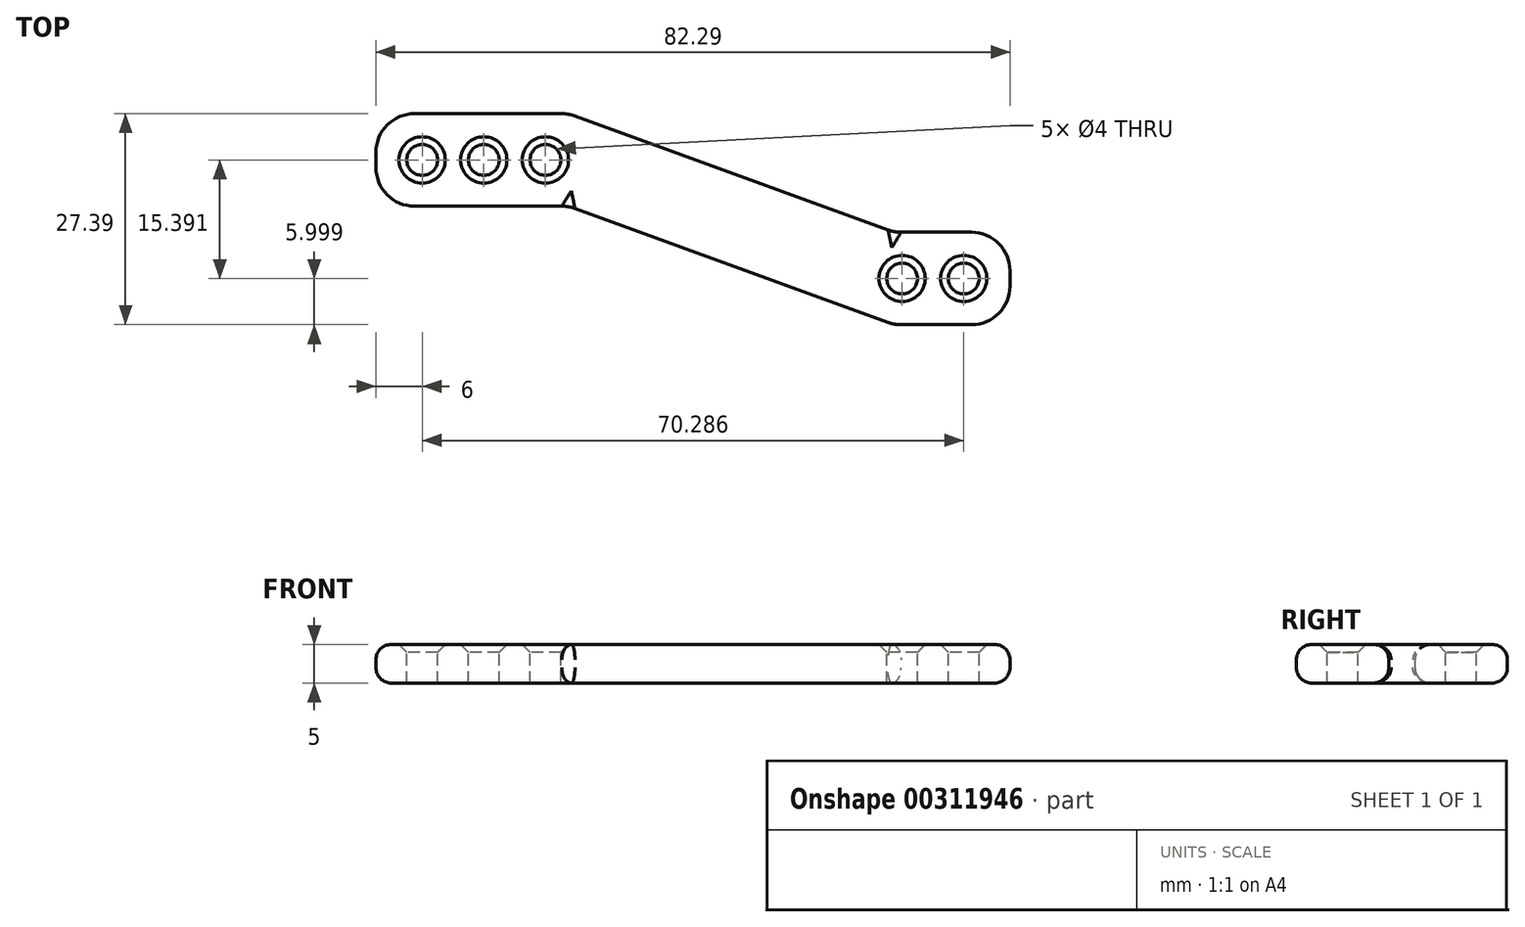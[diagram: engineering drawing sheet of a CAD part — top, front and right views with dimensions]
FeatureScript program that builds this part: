
annotation { "Feature Type Name" : "Feature", "Feature Type Description" : "" }
export const myFeature = defineFeature(function(context is Context, id is Id, definition is map)
    precondition{}
    {
        {
            var Q0;
            Q0=qCreatedBy(makeId("Top.planeOp"),FACE);
            var sketch = newSketch(context, id + "F0", { "sketchPlane" : qUnion([Q0])});
            skLineSegment(sketch, "E0.bottom", {"start": v(0, 0) * mm, "end": v(25, 0) * mm});
            skLineSegment(sketch, "E0.top", {"start": v(0, -12) * mm, "end": v(25, -12) * mm});
            skLineSegment(sketch, "E0.left", {"start": v(0, 0) * mm, "end": v(0, -12) * mm});
            skLineSegment(sketch, "E0.right", {"start": v(25, 0) * mm, "end": v(25, -12) * mm});
            skLineSegment(sketch, "E1.bottom", {"start": v(67.29, -15.4) * mm, "end": v(82.29, -15.4) * mm});
            skLineSegment(sketch, "E1.top", {"start": v(67.29, -27.4) * mm, "end": v(82.29, -27.4) * mm});
            skLineSegment(sketch, "E1.left", {"start": v(67.29, -15.4) * mm, "end": v(67.29, -27.4) * mm});
            skLineSegment(sketch, "E1.right", {"start": v(82.29, -15.4) * mm, "end": v(82.29, -27.4) * mm});
            skLineSegment(sketch, "E2", {"start": v(25, -12) * mm, "end": v(67.29, -27.4) * mm});
            skLineSegment(sketch, "E3", {"start": v(25, 0) * mm, "end": v(67.29, -15.4) * mm});
            skSolve(sketch);
        }
        {
            var Q0;
            Q0=makeQuery(id+"F0.imprint","IMPRINT",FACE,{"disambiguationData":[TD([[makeQuery(id+"F0.imprint","IMPRINT",EDGE,{"derivedFrom":sQuery(id+"F0.wireOp",EDGE,"E0.bottom")}),-1.0]])]});
            var Q1;
            Q1=makeQuery(id+"F0.imprint","IMPRINT",FACE,{"disambiguationData":[TD([[makeQuery(id+"F0.imprint","IMPRINT",EDGE,{"derivedFrom":sQuery(id+"F0.wireOp",EDGE,"E0.right")}),1.0]])]});
            var Q2;
            Q2=makeQuery(id+"F0.imprint","IMPRINT",FACE,{"disambiguationData":[TD([[makeQuery(id+"F0.imprint","IMPRINT",EDGE,{"derivedFrom":sQuery(id+"F0.wireOp",EDGE,"E1.bottom")}),-1.0]])]});
            extrude(context, id + "F1", {"entities" : qUnion([Q0, Q1, Q2]), "depth" : 5 * mm});
        }
        {
            var Q0;
            Q0=makeQuery(id+"F1.opExtrude","CAP_FACE",FACE,{"disambiguationData":[OSD([sQuery(id+"F0.wireOp",EDGE,"E0.bottom"),sQuery(id+"F0.wireOp",EDGE,"E0.top"),sQuery(id+"F0.wireOp",EDGE,"E0.left"),sQuery(id+"F0.wireOp",EDGE,"E1.bottom"),sQuery(id+"F0.wireOp",EDGE,"E1.top"),sQuery(id+"F0.wireOp",EDGE,"E1.right"),sQuery(id+"F0.wireOp",EDGE,"E2"),sQuery(id+"F0.wireOp",EDGE,"E3")])],"isStart":false});
            var sketch = newSketch(context, id + "F2", { "sketchPlane" : qUnion([Q0])});
            skCircle(sketch, "E4", {"center": v(6, -6) * mm, "radius": 2 * mm});
            skCircle(sketch, "E5", {"center": v(76.29, -21.4) * mm, "radius": 2 * mm});
            skCircle(sketch, "E6.1.0.0", {"center": v(14, -6) * mm, "radius": 2 * mm});
            skCircle(sketch, "E6.2.0.0", {"center": v(22, -6) * mm, "radius": 2 * mm});
            skLineSegment(sketch, "E6.direction1", {"start": v(6, -6) * mm, "end": v(14, -6) * mm, "construction": true});
            skCircle(sketch, "E7.1.0.0", {"center": v(68.29, -21.4) * mm, "radius": 2 * mm});
            skLineSegment(sketch, "E7.direction1", {"start": v(76.29, -21.4) * mm, "end": v(68.29, -21.4) * mm, "construction": true});
            skSolve(sketch);
        }
        {
            var Q0;
            Q0 = qSketchRegion(id + "F2", true);
            extrude(context, id + "F3", {"entities" : qUnion([Q0]), "operationType" : NewBodyOperationType.REMOVE, "oppositeDirection" : true, "depth" : 6 * mm});
        }
        {
            var Q0;
            Q0=makeQuery(id+"F1.opExtrude","CAP_EDGE",EDGE,{"disambiguationData":[OSD([sQuery(id+"F0.wireOp",EDGE,"E2")])],"isStart":false});
            var Q1;
            Q1=makeQuery(id+"F1.opExtrude","CAP_EDGE",EDGE,{"disambiguationData":[OSD([sQuery(id+"F0.wireOp",EDGE,"E0.top")])],"isStart":false});
            var Q2;
            Q2=makeQuery(id+"F1.opExtrude","CAP_EDGE",EDGE,{"disambiguationData":[OSD([sQuery(id+"F0.wireOp",EDGE,"E0.left")])],"isStart":false});
            var Q3;
            Q3=makeQuery(id+"F1.opExtrude","CAP_EDGE",EDGE,{"disambiguationData":[OSD([sQuery(id+"F0.wireOp",EDGE,"E0.bottom")])],"isStart":false});
            var Q4;
            Q4=makeQuery(id+"F1.opExtrude","CAP_EDGE",EDGE,{"disambiguationData":[OSD([sQuery(id+"F0.wireOp",EDGE,"E3")])],"isStart":false});
            var Q5;
            Q5=makeQuery(id+"F1.opExtrude","CAP_EDGE",EDGE,{"disambiguationData":[OSD([sQuery(id+"F0.wireOp",EDGE,"E1.bottom")])],"isStart":false});
            var Q6;
            Q6=makeQuery(id+"F1.opExtrude","CAP_EDGE",EDGE,{"disambiguationData":[OSD([sQuery(id+"F0.wireOp",EDGE,"E1.right")])],"isStart":false});
            var Q7;
            Q7=makeQuery(id+"F1.opExtrude","CAP_EDGE",EDGE,{"disambiguationData":[OSD([sQuery(id+"F0.wireOp",EDGE,"E1.top")])],"isStart":false});
            var Q8;
            Q8=makeQuery(id+"F1.opExtrude","CAP_EDGE",EDGE,{"disambiguationData":[OSD([sQuery(id+"F0.wireOp",EDGE,"E0.bottom")])],"isStart":true});
            var Q9;
            Q9=makeQuery(id+"F1.opExtrude","CAP_EDGE",EDGE,{"disambiguationData":[OSD([sQuery(id+"F0.wireOp",EDGE,"E0.left")])],"isStart":true});
            var Q10;
            Q10=makeQuery(id+"F1.opExtrude","CAP_EDGE",EDGE,{"disambiguationData":[OSD([sQuery(id+"F0.wireOp",EDGE,"E0.top")])],"isStart":true});
            var Q11;
            Q11=makeQuery(id+"F1.opExtrude","CAP_EDGE",EDGE,{"disambiguationData":[OSD([sQuery(id+"F0.wireOp",EDGE,"E2")])],"isStart":true});
            var Q12;
            Q12=makeQuery(id+"F1.opExtrude","CAP_EDGE",EDGE,{"disambiguationData":[OSD([sQuery(id+"F0.wireOp",EDGE,"E1.top")])],"isStart":true});
            var Q13;
            Q13=makeQuery(id+"F1.opExtrude","CAP_EDGE",EDGE,{"disambiguationData":[OSD([sQuery(id+"F0.wireOp",EDGE,"E1.bottom")])],"isStart":true});
            var Q14;
            Q14=makeQuery(id+"F1.opExtrude","CAP_EDGE",EDGE,{"disambiguationData":[OSD([sQuery(id+"F0.wireOp",EDGE,"E3")])],"isStart":true});
            var Q15;
            Q15=makeQuery(id+"F1.opExtrude","CAP_EDGE",EDGE,{"disambiguationData":[OSD([sQuery(id+"F0.wireOp",EDGE,"E1.right")])],"isStart":true});
            fillet(context, id + "F4", {"entities" : qUnion([Q0, Q1, Q2, Q3, Q4, Q5, Q6, Q7, Q8, Q9, Q10, Q11, Q12, Q13, Q14, Q15]), "radius" : 2 * mm, "tangentPropagation" : true, "allowEdgeOverflow" : false});
        }
        {
            var Q0;
            Q0=makeQuery(id+"F1.opExtrude","SWEPT_EDGE",EDGE,{"disambiguationData":[OSD([sQuery(id+"F0.wireOp",EDGE,"E1.top"),sQuery(id+"F0.wireOp",EDGE,"E1.right")])]});
            var Q1;
            Q1=makeQuery(id+"F1.opExtrude","SWEPT_EDGE",EDGE,{"disambiguationData":[OSD([sQuery(id+"F0.wireOp",EDGE,"E1.bottom"),sQuery(id+"F0.wireOp",EDGE,"E1.right")])]});
            var Q2;
            Q2=makeQuery(id+"F1.opExtrude","SWEPT_EDGE",EDGE,{"disambiguationData":[OSD([sQuery(id+"F0.wireOp",EDGE,"E0.bottom"),sQuery(id+"F0.wireOp",EDGE,"E0.left")])]});
            var Q3;
            Q3=makeQuery(id+"F1.opExtrude","SWEPT_EDGE",EDGE,{"disambiguationData":[OSD([sQuery(id+"F0.wireOp",EDGE,"E0.top"),sQuery(id+"F0.wireOp",EDGE,"E0.left")])]});
            var Q4;
            Q4=makeQuery(id+"F1.opExtrude","SWEPT_EDGE",EDGE,{"disambiguationData":[OSD([sQuery(id+"F0.wireOp",EDGE,"E0.top"),sQuery(id+"F0.wireOp",EDGE,"E0.right"),sQuery(id+"F0.wireOp",EDGE,"E2")])]});
            var Q5;
            Q5=makeQuery(id+"F1.opExtrude","SWEPT_EDGE",EDGE,{"disambiguationData":[OSD([sQuery(id+"F0.wireOp",EDGE,"E1.top"),sQuery(id+"F0.wireOp",EDGE,"E1.left"),sQuery(id+"F0.wireOp",EDGE,"E2")])]});
            var Q6;
            Q6=makeQuery(id+"F1.opExtrude","SWEPT_EDGE",EDGE,{"disambiguationData":[OSD([sQuery(id+"F0.wireOp",EDGE,"E1.bottom"),sQuery(id+"F0.wireOp",EDGE,"E1.left"),sQuery(id+"F0.wireOp",EDGE,"E3")])]});
            var Q7;
            Q7=makeQuery(id+"F1.opExtrude","SWEPT_EDGE",EDGE,{"disambiguationData":[OSD([sQuery(id+"F0.wireOp",EDGE,"E0.bottom"),sQuery(id+"F0.wireOp",EDGE,"E0.right"),sQuery(id+"F0.wireOp",EDGE,"E3")])]});
            fillet(context, id + "F5", {"entities" : qUnion([Q0, Q1, Q2, Q3, Q4, Q5, Q6, Q7]), "radius" : 5 * mm, "tangentPropagation" : true, "allowEdgeOverflow" : false});
        }
        {
            var Q0;
            Q0=makeQuery(id+"F1.opExtrude","CAP_FACE",FACE,{"disambiguationData":[OSD([sQuery(id+"F0.wireOp",EDGE,"E0.bottom"),sQuery(id+"F0.wireOp",EDGE,"E0.top"),sQuery(id+"F0.wireOp",EDGE,"E0.left"),sQuery(id+"F0.wireOp",EDGE,"E1.bottom"),sQuery(id+"F0.wireOp",EDGE,"E1.top"),sQuery(id+"F0.wireOp",EDGE,"E1.right"),sQuery(id+"F0.wireOp",EDGE,"E2"),sQuery(id+"F0.wireOp",EDGE,"E3")])],"isStart":false});
            chamfer(context, id + "F6", {"entities" : qUnion([Q0]), "width" : 1 * mm, "tangentPropagation" : true});
        }
    });
